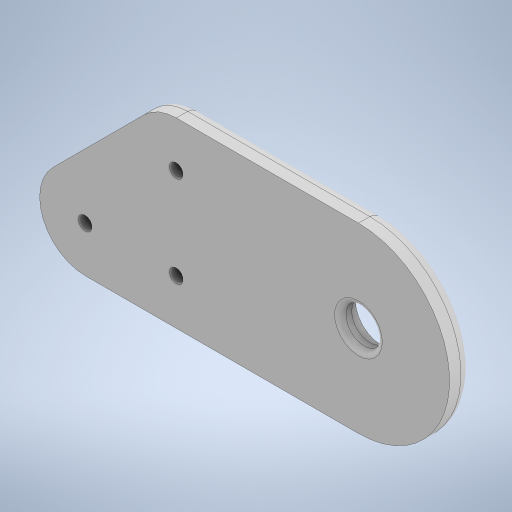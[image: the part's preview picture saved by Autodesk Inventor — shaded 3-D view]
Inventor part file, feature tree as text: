
AUTODESK INVENTOR PART (.ipt)
format: ipt  version: 2024 (Build 280153000, 153)  size: 313,344 bytes
history: native  units: in
note: dims shown in document units (in); Inventor stores cm internally (conversion verified against a paired STEP export)
features: extrude x6, sketch x4, fillet x3, projected_geometry x3
ambient origin geometry x8: Origin, YZ Plane, XZ Plane, XY Plane, X Axis, Y Axis, Z Axis, Center Point
bodies: Solid1 (feature_tree)
feature tree (16):
  extrude  "Extrusion1"  Depth=2.0in
  sketch  "Sketch2"  dims[d2=0.25in d3=0.0in d4=0.15in]
  extrude  "Extrusion2"  Depth=0.25in
  extrude  "Extrusion3"  Depth=1.0in
  sketch  "Sketch7"  dims[d5=0.35in d6=1.0in]
  extrude  "Extrusion9"  Depth=0.5in
  extrude  "Extrusion10"  Depth=0.5in
  extrude  "Extrusion11"  TaperAngle=0.0deg  [1 undecoded]
  fillet  "Fillet5"  Radius=0.125in
  fillet  "Fillet6"  Radius=1.0in
  fillet  "Fillet7"  Radius=0.57in
  sketch  "Sketch1"  dims[d0=4.5in d1=2.0in]
  projected_geometry  "Projected Loop1"
  projected_geometry  "Projected Loop7"
  sketch  "Sketch8"  dims[d7=1.0in d8=0.5in d10=0.5in d12=0.0in d13=0.0in d14=0.125in d15=0.0in d40=1.0in d41=0.57in d42=0.4in d43=0.09in d44=0.5in d45=0.5in d46=0.0in d47=0.0in d48=0.125in d49=0.0in d50=0.0in d51=0.0in d52=0.0625in d53=0.0625in d54=0.125in]
  projected_geometry  "Projected Loop8"
note: 1 required parameter value undecoded (feature->parameter linkage not recoverable at this tier; creation-order binding heuristic only, values carry confidence <= 0.55)
